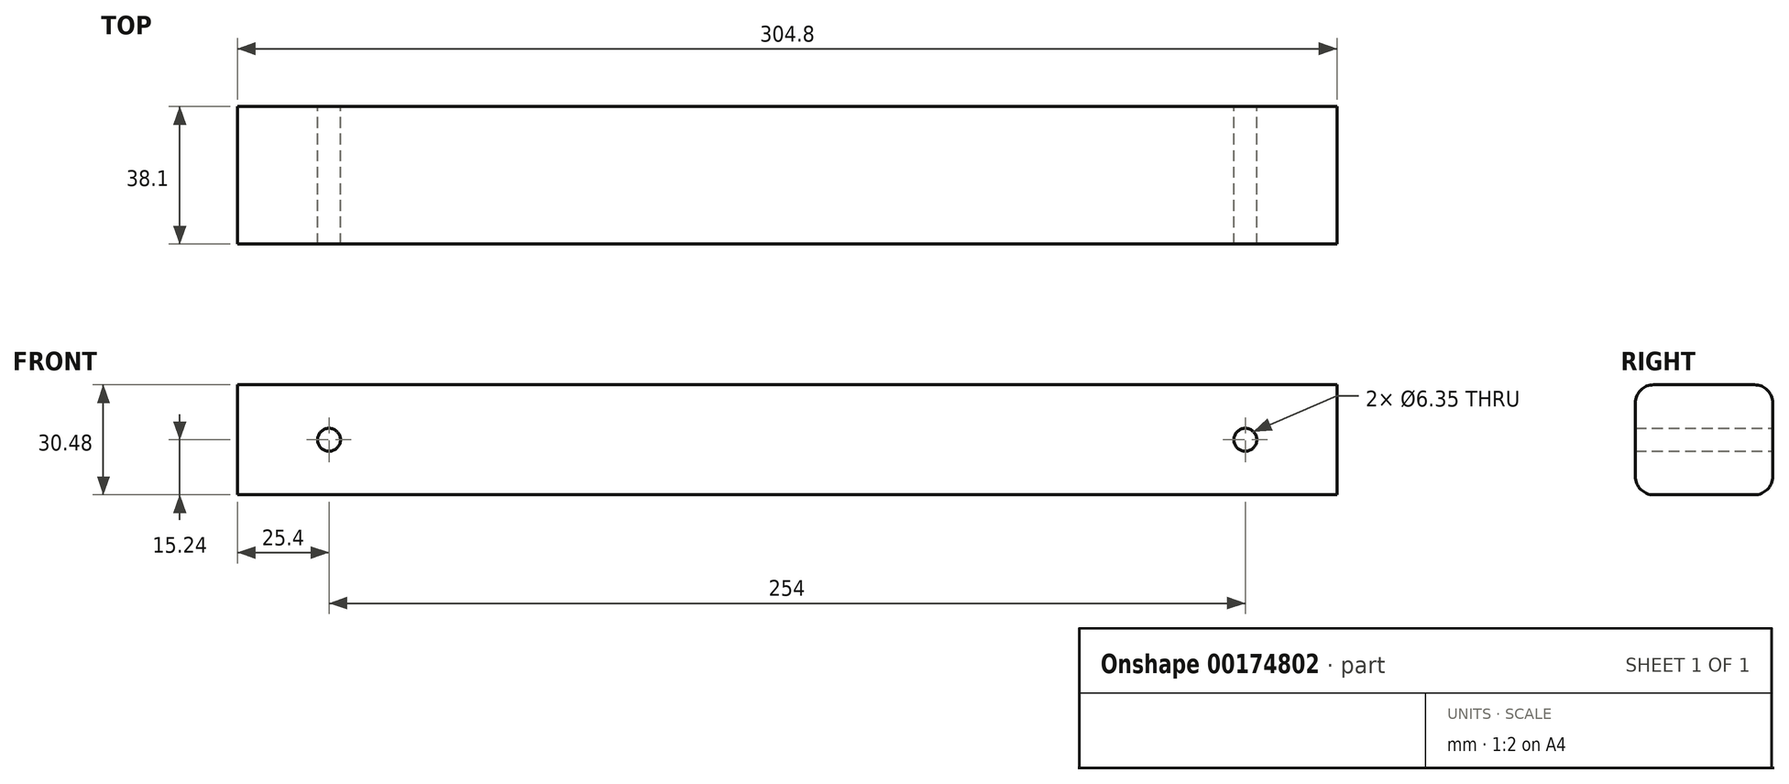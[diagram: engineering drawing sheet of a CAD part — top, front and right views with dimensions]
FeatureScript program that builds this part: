
annotation { "Feature Type Name" : "Feature", "Feature Type Description" : "" }
export const myFeature = defineFeature(function(context is Context, id is Id, definition is map)
    precondition{}
    {
        {
            var Q0;
            Q0=qCreatedBy(makeId("Front.planeOp"),FACE);
            var sketch = newSketch(context, id + "F0", { "sketchPlane" : qUnion([Q0])});
            skLineSegment(sketch, "E0.bottom", {"start": v(-152.4, -15.24) * mm, "end": v(152.4, -15.24) * mm});
            skLineSegment(sketch, "E0.top", {"start": v(-152.4, 15.24) * mm, "end": v(152.4, 15.24) * mm});
            skLineSegment(sketch, "E0.left", {"start": v(-152.4, -15.24) * mm, "end": v(-152.4, 15.24) * mm});
            skLineSegment(sketch, "E0.right", {"start": v(152.4, -15.24) * mm, "end": v(152.4, 15.24) * mm});
            skPoint(sketch, "E0.middle", {"position": v(0, 0) * mm});
            skCircle(sketch, "E1", {"center": v(-127, 0) * mm, "radius": 3.18 * mm});
            skCircle(sketch, "E2", {"center": v(127, 0) * mm, "radius": 3.18 * mm});
            skPoint(sketch, "E3.orphan", {"position": v(152.4, 0) * mm});
            skPoint(sketch, "E4.trimOffspring.end.orphan", {"position": v(-152.4, 0) * mm});
            skSolve(sketch);
        }
        {
            var Q0;
            Q0 = qSketchRegion(id + "F0", true);
            extrude(context, id + "F1", {"entities" : qUnion([Q0]), "depth" : 38.1 * mm});
        }
        {
            var Q0;
            Q0=makeQuery(id+"F1.opExtrude","CAP_EDGE",EDGE,{"disambiguationData":[OSD([sQuery(id+"F0.wireOp",EDGE,"E0.top")])],"isStart":true});
            var Q1;
            Q1=makeQuery(id+"F1.opExtrude","CAP_EDGE",EDGE,{"disambiguationData":[OSD([sQuery(id+"F0.wireOp",EDGE,"E0.top")])],"isStart":false});
            var Q2;
            Q2=makeQuery(id+"F1.opExtrude","CAP_EDGE",EDGE,{"disambiguationData":[OSD([sQuery(id+"F0.wireOp",EDGE,"E0.bottom")])],"isStart":true});
            var Q3;
            Q3=makeQuery(id+"F1.opExtrude","CAP_EDGE",EDGE,{"disambiguationData":[OSD([sQuery(id+"F0.wireOp",EDGE,"E0.bottom")])],"isStart":false});
            fillet(context, id + "F2", {"entities" : qUnion([Q0, Q1, Q2, Q3]), "radius" : 5.08 * mm, "tangentPropagation" : true, "allowEdgeOverflow" : false});
        }
    });
